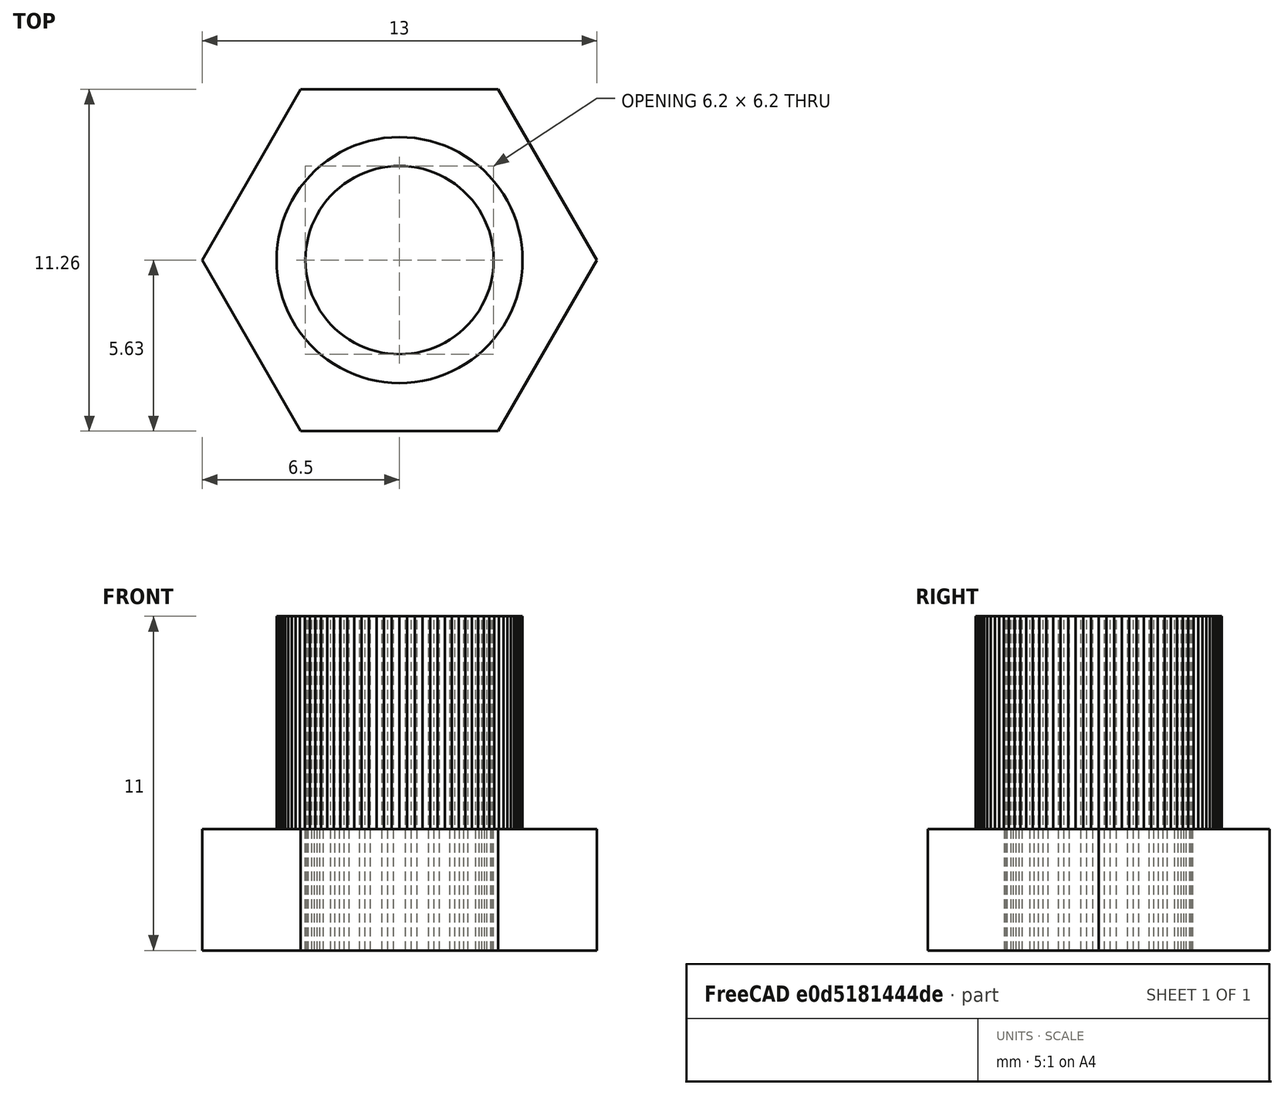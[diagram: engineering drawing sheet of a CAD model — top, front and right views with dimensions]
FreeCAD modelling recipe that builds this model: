
FCSTD DOCUMENT  (FreeCAD 0.19R17798 (Git))
Label: shaftadapter_6_8mm
License: All rights reserved
LicenseURL: http://en.wikipedia.org/wiki/All_rights_reserved
objects: Part::Prism×4, Part::Cut×2, Part::Fuse×1
note: 7 computed .brp shape members not serialized (recipe doc carries the construction recipe); baked Part::Feature solids carry a one-line shape summary decoded from their .brp

FEATURE [Part::Prism] prism
  AttacherType = Attacher::AttachEngine3D
  Circumradius = 4.05
  Height = 11
  Placement = pos=(0,0,-5.5) rot=(0,0,1;0rad)
  Polygon = 100
FEATURE [Part::Prism] prism001
  AttacherType = Attacher::AttachEngine3D
  Circumradius = 3.1
  Height = 11.05
  Placement = pos=(0,0,-5.525) rot=(0,0,1;0rad)
  Polygon = 100
FEATURE [Part::Cut] difference
  Base = -> prism
  Placement = pos=(0,0,5.5) rot=(0,0,1;0rad)
  Refine = true
  Tool = -> prism001
FEATURE [Part::Prism] prism002
  AttacherType = Attacher::AttachEngine3D
  Circumradius = 6.5
  Height = 4
  Placement = pos=(0,0,-2) rot=(0,0,1;0rad)
  Polygon = 6
FEATURE [Part::Prism] prism003
  AttacherType = Attacher::AttachEngine3D
  Circumradius = 3.1
  Height = 11.05
  Placement = pos=(0,0,-5.525) rot=(0,0,1;0rad)
  Polygon = 100
FEATURE [Part::Cut] difference001
  Base = -> prism002
  Placement = pos=(0,0,2) rot=(0,0,1;0rad)
  Refine = true
  Tool = -> prism003
FEATURE [Part::Fuse] Group
  Base = -> difference
  Refine = true
  Tool = -> difference001
